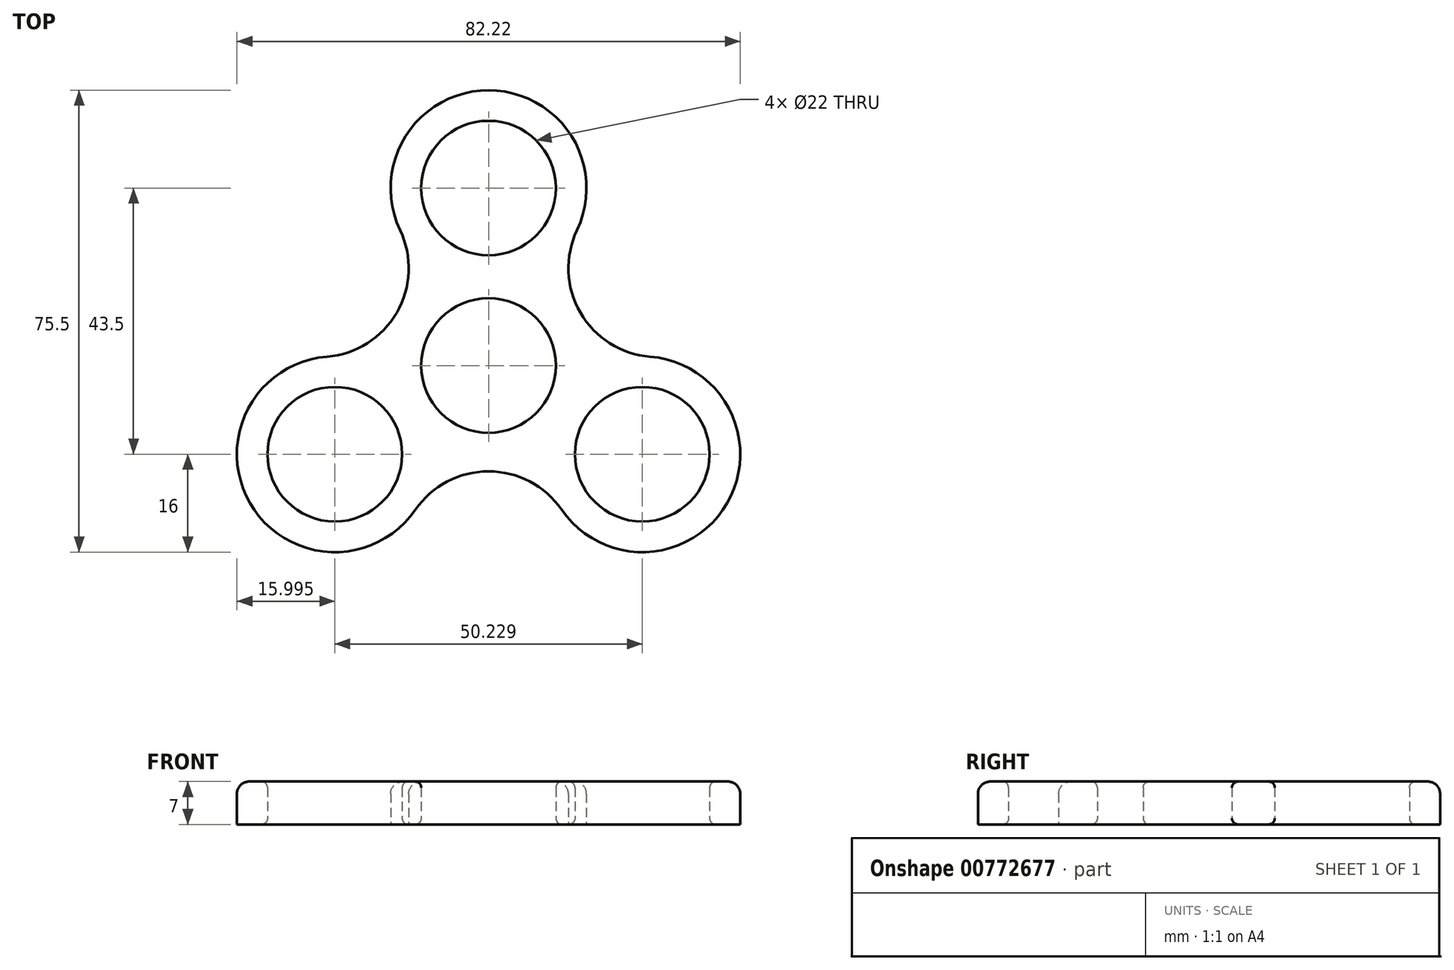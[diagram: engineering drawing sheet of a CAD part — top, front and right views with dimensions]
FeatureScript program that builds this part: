
annotation { "Feature Type Name" : "Feature", "Feature Type Description" : "" }
export const myFeature = defineFeature(function(context is Context, id is Id, definition is map)
    precondition{}
    {
        {
            var Q0;
            Q0=qCreatedBy(makeId("Top.planeOp"),FACE);
            var sketch = newSketch(context, id + "F0", { "sketchPlane" : qUnion([Q0])});
            skCircle(sketch, "E0", {"center": v(0, 0) * mm, "radius": 11 * mm});
            skCircle(sketch, "E1", {"center": v(0, 29) * mm, "radius": 11 * mm});
            skCircle(sketch, "E2.1.0", {"center": v(-25.11, -14.5) * mm, "radius": 11 * mm});
            skCircle(sketch, "E2.2.0", {"center": v(25.11, -14.5) * mm, "radius": 11 * mm});
            skArc(sketch, "E3", {"start": v(14.45, 22.13) * mm, "mid": v(0, 45) * mm, "end": v(-14.45, 22.13) * mm});
            skArc(sketch, "E4.1.0", {"start": v(-26.39, 1.45) * mm, "mid": v(-38.97, -22.5) * mm, "end": v(-11.94, -23.58) * mm});
            skArc(sketch, "E4.2.0", {"start": v(11.94, -23.58) * mm, "mid": v(38.97, -22.5) * mm, "end": v(26.39, 1.45) * mm});
            skArc(sketch, "E5", {"start": v(14.45, 22.13) * mm, "mid": v(14.99, 8.65) * mm, "end": v(26.39, 1.45) * mm});
            skArc(sketch, "E6.1.0", {"start": v(-26.39, 1.45) * mm, "mid": v(-14.99, 8.65) * mm, "end": v(-14.45, 22.13) * mm});
            skArc(sketch, "E6.2.0", {"start": v(11.94, -23.58) * mm, "mid": v(0, -17.3) * mm, "end": v(-11.94, -23.58) * mm});
            skSolve(sketch);
        }
        {
            var Q0;
            Q0=qSketchRegion(id+"F0",true);
            extrude(context, id + "F1", {"entities" : qUnion([Q0]), "depth" : 7 * mm, "offsetDistance" : 25 * mm});
        }
        {
            var Q0;
            Q0=makeQuery(id+"F1.opExtrude","CAP_EDGE",EDGE,{"disambiguationData":[OSD([sQuery(id+"F0.wireOp",EDGE,"E1")])],"isStart":false});
            var Q1;
            Q1=makeQuery(id+"F1.opExtrude","CAP_EDGE",EDGE,{"disambiguationData":[OSD([sQuery(id+"F0.wireOp",EDGE,"E0")])],"isStart":false});
            var Q2;
            Q2=makeQuery(id+"F1.opExtrude","CAP_EDGE",EDGE,{"disambiguationData":[OSD([sQuery(id+"F0.wireOp",EDGE,"E2.2.0")])],"isStart":false});
            var Q3;
            Q3=makeQuery(id+"F1.opExtrude","CAP_EDGE",EDGE,{"disambiguationData":[OSD([sQuery(id+"F0.wireOp",EDGE,"E2.1.0")])],"isStart":false});
            var Q4;
            Q4=makeQuery(id+"F1.opExtrude","CAP_EDGE",EDGE,{"disambiguationData":[OSD([sQuery(id+"F0.wireOp",EDGE,"E2.1.0")])],"isStart":true});
            var Q5;
            Q5=makeQuery(id+"F1.opExtrude","CAP_EDGE",EDGE,{"disambiguationData":[OSD([sQuery(id+"F0.wireOp",EDGE,"E0")])],"isStart":true});
            var Q6;
            Q6=makeQuery(id+"F1.opExtrude","CAP_EDGE",EDGE,{"disambiguationData":[OSD([sQuery(id+"F0.wireOp",EDGE,"E2.2.0")])],"isStart":true});
            var Q7;
            Q7=makeQuery(id+"F1.opExtrude","CAP_EDGE",EDGE,{"disambiguationData":[OSD([sQuery(id+"F0.wireOp",EDGE,"E1")])],"isStart":true});
            fillet(context, id + "F2", {"entities" : qUnion([Q0, Q1, Q2, Q3, Q4, Q5, Q6, Q7]), "radius" : 1 * mm, "tangentPropagation" : true, "allowEdgeOverflow" : false});
        }
        {
            var Q0;
            Q0=makeQuery(id+"F1.opExtrude","CAP_EDGE",EDGE,{"disambiguationData":[OSD([sQuery(id+"F0.wireOp",EDGE,"E6.1.0")])],"isStart":false});
            fillet(context, id + "F3", {"entities" : qUnion([Q0]), "radius" : 2 * mm, "tangentPropagation" : true, "allowEdgeOverflow" : false});
        }
    });
